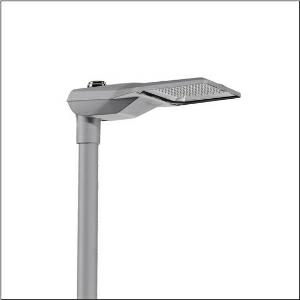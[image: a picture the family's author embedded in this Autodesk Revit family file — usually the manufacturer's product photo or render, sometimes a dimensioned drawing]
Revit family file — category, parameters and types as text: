
# Revit family: streetlight_sl_21_midi___st1_0a_5xe7d67n08nb_5be6
name_source: partatom
category: Lighting Fixtures
units: mm (PartAtom-declared; Revit-internal decimal feet)

## family parameters
Cut with Voids When Loaded = No
Host = Face
Light Source = No
Part Type = Normal
Room Calculation Point = No
Round Connector Dimension = Use Diameter
Shared = No

## types (1)
- --- (1 x LED, 20350 lm, 151.2 W, 2700K)
    Apparent Load = 151 VA
    CIE Flux Codes = 40 73 97 100 100
    Color Rendering = 70
    Color Temperature = 2700K
    Default Elevation = 1800 mm
    Description = Streetlight SL 21 midi, mast luminaire, primary light control with lens, of PMMA, primary optical cover: cover, of toughened safety glass, transparent, light distribution: ST1.0a, light emission: direct distribution, primary light characteristic: asymmetric, installation type: side-entry, LED, 3G 2.5mm², High Power LED, rated luminous flux: 20.350lm, luminous efficacy: 135lm/W, light colour: 727, colour temperature: 2700K, control gear: NEMA (7pin), control: overheat protection, pre-setting: linear dimming characteristic, constant luminous flux control, time-dependent luminous flux control, flexible luminous flux parameterisation, mains connection: 220..240V, AC, 50/60Hz, connection cable pre-assembled, cable length: 12,5m, wiring characteristics: H05VV-F, start of lifetime: 151W, end of service life: 157W, reduction: 70W, luminaire housing, of diecast aluminium (EN AC-44300), powder-coated, SITECO metallic grey (DB 702S), corrosivity category C5 high according to DIN EN ISO 12944, multi-level sealing system, sealing non-destructively replaceable, inclination adjustable: 0°, 5°, 10°, 15°, length: 644mm, width: 335mm, height: 110mm, spigot size: 42mm (side-entry), mounting height: 4..8m, protection rating (complete): IP66, insulation class (complete): insulation class I (protective earthing), certification: CE, ENEC, ENEC+, VDE, impact resistance: IK10, permissible operating ambient temperature for outdoor applications: -40..+50°C, standard-compliant lighting for roads and squares, packaging unit: 1 piece

Light Distribution: ST1.0a
    Height = 111 mm
    Lamp = 1 x LED
    Lamp Light Flux = 20350 lm
    Lamp Power = 151.2 W
    Lamp count = 1
    Length = 644 mm
    Luminous efficacy = 135 lm/W
    Manufacturer = Siteco
    ModVariant = No
    Model = 5XE7D67N08NB
    Number of Poles = 1
    OnlyDefault = Yes
    Power Factor = 1
    Product Name = Streetlight SL 21 midi | ST1.0a
    Product group = mast luminaire | pylon top
    ProductGroupID = 6100
    Protection Class = Protection class I
    Protection Degree = IP 66
    RLX_Detail_Level = 1
    RLX_Emergency_Light_Flux = 0 lm
    RLX_Emergency_Type = 0
    RLX_Emergency_Type_DB = No
    RlxData = <blob elided: 26709 chars, md5=781a1e38>
    Socket = socket
    Standby Power = 0 W
    System Light Flux = 20350 lm
    System Power = 151 W
    Type Comments = factory setting: luminous flux: 100 % | dim-lin: 254 | 802 mA
    Type Image = l_1294377.jpg
    URL = http://relux.com
    VarID = @adj_134547
    Voltage = 0 V
    Weight = 0.00 kg
    Width = 336 mm

## geometry (parser evidence)
native form markers: Blend x4, Sweep x11
no freeform markers — native parametric forms only
